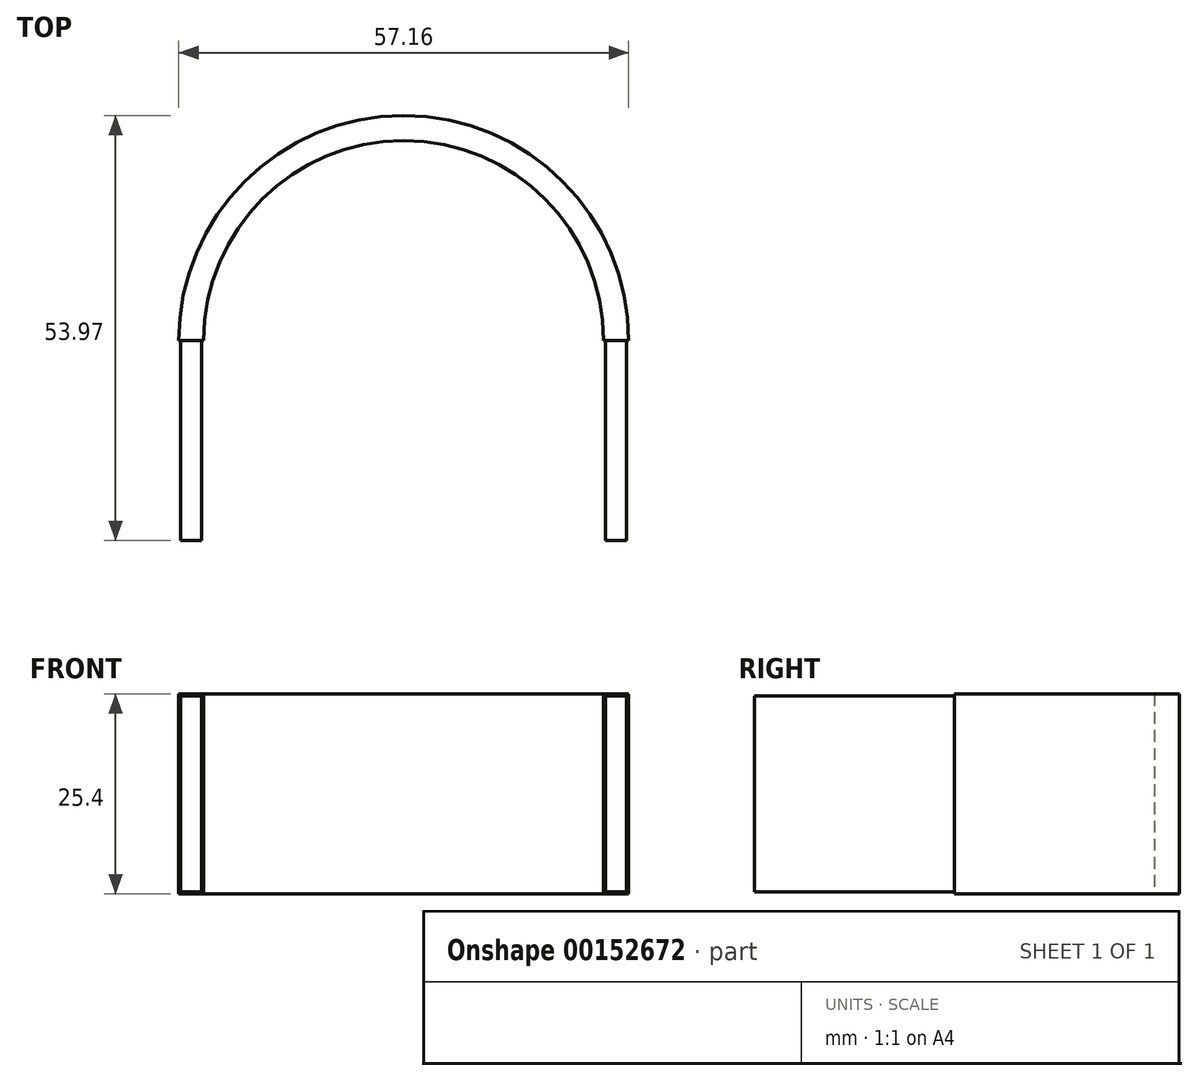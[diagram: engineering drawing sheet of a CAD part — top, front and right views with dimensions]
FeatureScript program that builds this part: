
annotation { "Feature Type Name" : "Feature", "Feature Type Description" : "" }
export const myFeature = defineFeature(function(context is Context, id is Id, definition is map)
    precondition{}
    {
        {
            var Q0;
            Q0=qCreatedBy(makeId("Top.planeOp"),FACE);
            var sketch = newSketch(context, id + "F0", { "sketchPlane" : qUnion([Q0])});
            skLineSegment(sketch, "E0.bottom", {"start": v(0, 0) * mm, "end": v(-3.18, 0) * mm});
            skLineSegment(sketch, "E0.top", {"start": v(0, 25.4) * mm, "end": v(-3.18, 25.4) * mm, "construction": true});
            skLineSegment(sketch, "E0.left", {"start": v(0, 0) * mm, "end": v(0, 25.4) * mm});
            skLineSegment(sketch, "E0.right", {"start": v(-3.17, 0) * mm, "end": v(-3.18, 25.4) * mm});
            skLineSegment(sketch, "E1", {"start": v(0, 25.4) * mm, "end": v(50.8, 25.4) * mm, "construction": true});
            skLineSegment(sketch, "E2.bottom", {"start": v(50.8, 25.4) * mm, "end": v(53.97, 25.4) * mm, "construction": true});
            skLineSegment(sketch, "E2.top", {"start": v(50.8, 0) * mm, "end": v(53.98, 0) * mm});
            skLineSegment(sketch, "E2.left", {"start": v(50.8, 25.4) * mm, "end": v(50.8, 0) * mm});
            skLineSegment(sketch, "E2.right", {"start": v(53.98, 25.4) * mm, "end": v(53.98, 0) * mm});
            skArc(sketch, "E3", {"start": v(50.8, 25.4) * mm, "mid": v(25.4, 50.8) * mm, "end": v(0, 25.4) * mm});
            skArc(sketch, "E4", {"start": v(53.98, 25.4) * mm, "mid": v(25.4, 53.98) * mm, "end": v(-3.18, 25.4) * mm});
            skSolve(sketch);
        }
        {
            var Q0;
            Q0=qSketchRegion(id+"F0",true);
            extrude(context, id + "F1", {"entities" : qUnion([Q0]), "depth" : 25.4 * mm});
        }
        {
            var Q0;
            Q0=makeQuery(id+"F1.opExtrude","CAP_FACE",FACE,{"disambiguationData":[OSD([sQuery(id+"F0.wireOp",EDGE,"E0.bottom"),sQuery(id+"F0.wireOp",EDGE,"E0.left"),sQuery(id+"F0.wireOp",EDGE,"E0.right"),sQuery(id+"F0.wireOp",EDGE,"E2.top"),sQuery(id+"F0.wireOp",EDGE,"E2.left"),sQuery(id+"F0.wireOp",EDGE,"E2.right"),sQuery(id+"F0.wireOp",EDGE,"E3"),sQuery(id+"F0.wireOp",EDGE,"E4")])],"isStart":false});
            var sketch = newSketch(context, id + "F2", { "sketchPlane" : qUnion([Q0])});
            skLineSegment(sketch, "E5.bottom", {"start": v(-3.17, 0) * mm, "end": v(-2.92, 0) * mm});
            skLineSegment(sketch, "E5.top", {"start": v(-3.18, 25.4) * mm, "end": v(-2.92, 25.4) * mm});
            skLineSegment(sketch, "E5.left", {"start": v(-3.17, 0) * mm, "end": v(-3.17, 25.4) * mm});
            skLineSegment(sketch, "E5.right", {"start": v(-2.92, 0) * mm, "end": v(-2.92, 25.4) * mm});
            skSolve(sketch);
        }
        {
            var Q0;
            Q0=makeQuery(id+"F2.imprint","IMPRINT",FACE,{"disambiguationData":[TD([[makeQuery(id+"F2.imprint","IMPRINT",EDGE,{"derivedFrom":sQuery(id+"F2.wireOp",EDGE,"E5.bottom")}),-1.0]])]});
            var Q1;
            Q1=makeQuery(id+"F1.opExtrude","SWEPT_EDGE",EDGE,{"disambiguationData":[OSD([sQuery(id+"F0.wireOp",EDGE,"E0.bottom"),sQuery(id+"F0.wireOp",EDGE,"E0.right")])]});
            var Q2;
            Q2=makeQuery(id+"F1.opExtrude","CAP_EDGE",EDGE,{"disambiguationData":[OSD([sQuery(id+"F0.wireOp",EDGE,"E0.bottom")])],"isStart":true});
            var Q3;
            Q3=makeQuery(id+"F1.opExtrude","SWEPT_EDGE",EDGE,{"disambiguationData":[OSD([sQuery(id+"F0.wireOp",EDGE,"E0.bottom"),sQuery(id+"F0.wireOp",EDGE,"E0.left")])]});
            var Q4;
            Q4=makeQuery(id+"F1.opExtrude","CAP_EDGE",EDGE,{"disambiguationData":[OSD([sQuery(id+"F0.wireOp",EDGE,"E0.bottom")])],"isStart":false});
            sweep(context, id + "F3", {"operationType" : NewBodyOperationType.REMOVE, "profiles" : qUnion([Q0]), "path" : qUnion([Q1, Q2, Q3, Q4])});
        }
        {
            var Q0;
            Q0=makeQuery(id+"F1.opExtrude","CAP_FACE",FACE,{"disambiguationData":[OSD([sQuery(id+"F0.wireOp",EDGE,"E0.bottom"),sQuery(id+"F0.wireOp",EDGE,"E0.left"),sQuery(id+"F0.wireOp",EDGE,"E0.right"),sQuery(id+"F0.wireOp",EDGE,"E2.top"),sQuery(id+"F0.wireOp",EDGE,"E2.left"),sQuery(id+"F0.wireOp",EDGE,"E2.right"),sQuery(id+"F0.wireOp",EDGE,"E3"),sQuery(id+"F0.wireOp",EDGE,"E4")])],"isStart":false});
            var sketch = newSketch(context, id + "F4", { "sketchPlane" : qUnion([Q0])});
            skLineSegment(sketch, "E6.bottom", {"start": v(50.8, 0) * mm, "end": v(51.05, 0) * mm});
            skLineSegment(sketch, "E6.top", {"start": v(50.8, 25.4) * mm, "end": v(51.05, 25.4) * mm});
            skLineSegment(sketch, "E6.left", {"start": v(50.8, 0) * mm, "end": v(50.8, 25.4) * mm});
            skLineSegment(sketch, "E6.right", {"start": v(51.05, 0) * mm, "end": v(51.05, 25.4) * mm});
            skSolve(sketch);
        }
        {
            var Q0;
            Q0=makeQuery(id+"F4.imprint","IMPRINT",FACE,{"disambiguationData":[TD([[makeQuery(id+"F4.imprint","IMPRINT",EDGE,{"derivedFrom":sQuery(id+"F4.wireOp",EDGE,"E6.bottom")}),1.0]])]});
            var Q1;
            Q1=makeQuery(id+"F1.opExtrude","SWEPT_EDGE",EDGE,{"disambiguationData":[OSD([sQuery(id+"F0.wireOp",EDGE,"E2.top"),sQuery(id+"F0.wireOp",EDGE,"E2.left")])]});
            var Q2;
            Q2=makeQuery(id+"F1.opExtrude","CAP_EDGE",EDGE,{"disambiguationData":[OSD([sQuery(id+"F0.wireOp",EDGE,"E2.top")])],"isStart":true});
            var Q3;
            Q3=makeQuery(id+"F1.opExtrude","SWEPT_EDGE",EDGE,{"disambiguationData":[OSD([sQuery(id+"F0.wireOp",EDGE,"E2.top"),sQuery(id+"F0.wireOp",EDGE,"E2.right")])]});
            var Q4;
            Q4=makeQuery(id+"F1.opExtrude","CAP_EDGE",EDGE,{"disambiguationData":[OSD([sQuery(id+"F0.wireOp",EDGE,"E2.top")])],"isStart":false});
            sweep(context, id + "F5", {"operationType" : NewBodyOperationType.REMOVE, "profiles" : qUnion([Q0]), "path" : qUnion([Q1, Q2, Q3, Q4])});
        }
    });
